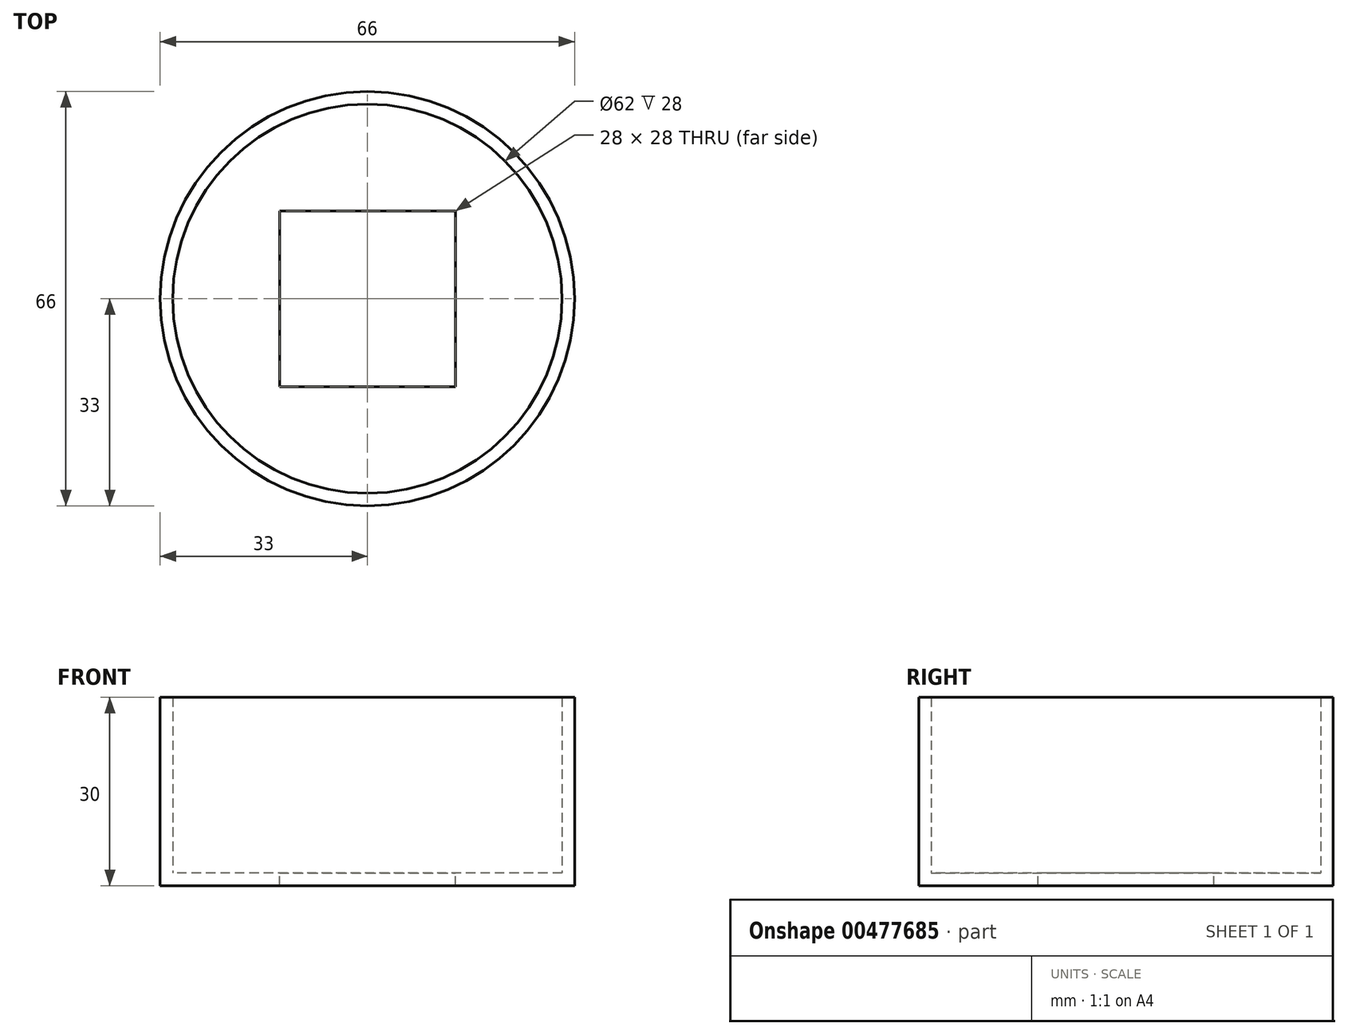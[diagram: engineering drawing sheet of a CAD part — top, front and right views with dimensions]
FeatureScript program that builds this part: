
annotation { "Feature Type Name" : "Feature", "Feature Type Description" : "" }
export const myFeature = defineFeature(function(context is Context, id is Id, definition is map)
    precondition{}
    {
        {
            var Q0;
            Q0=qCreatedBy(makeId("Top.planeOp"),FACE);
            var sketch = newSketch(context, id + "F0", { "sketchPlane" : qUnion([Q0])});
            skCircle(sketch, "E0", {"center": v(0, 0) * mm, "radius": 33 * mm});
            skSolve(sketch);
        }
        {
            var Q0;
            Q0=qSketchRegion(id+"F0",true);
            extrude(context, id + "F1", {"entities" : qUnion([Q0]), "depth" : 30 * mm});
        }
        {
            var Q0;
            Q0=makeQuery(id+"F1.opExtrude","CAP_FACE",FACE,{"disambiguationData":[OSD([sQuery(id+"F0.wireOp",EDGE,"E0")])],"isStart":false});
            shell(context, id + "F2", {"entities" : qUnion([Q0]), "thickness" : 2 * mm});
        }
        {
            var Q0;
            Q0=qSketchRegion(id+"F0",true);
            extrude(context, id + "F3", {"entities" : qUnion([Q0]), "operationType" : NewBodyOperationType.REMOVE, "endBound" : BoundingType.THROUGH_ALL, "oppositeDirection" : true, "depth" : 25 * mm});
        }
        {
            var Q0;
            Q0=makeQuery(id+"F0.imprint","IMPRINT",FACE,{"disambiguationData":[TD([[makeQuery(id+"F0.imprint","IMPRINT",EDGE,{"derivedFrom":sQuery(id+"F0.wireOp",EDGE,"E0")}),1.0]])]});
            var sketch = newSketch(context, id + "F4", { "sketchPlane" : qUnion([Q0])});
            skLineSegment(sketch, "E1.bottom", {"start": v(-14, 14) * mm, "end": v(14, 14) * mm});
            skLineSegment(sketch, "E1.top", {"start": v(-14, -14) * mm, "end": v(14, -14) * mm});
            skLineSegment(sketch, "E1.left", {"start": v(-14, 14) * mm, "end": v(-14, -14) * mm});
            skLineSegment(sketch, "E1.right", {"start": v(14, 14) * mm, "end": v(14, -14) * mm});
            skPoint(sketch, "E1.middle", {"position": v(0, 0) * mm});
            skSolve(sketch);
        }
        {
            var Q0;
            Q0=makeQuery(id+"F4.imprint","IMPRINT",FACE,{"disambiguationData":[TD([[makeQuery(id+"F4.imprint","IMPRINT",EDGE,{"derivedFrom":sQuery(id+"F4.wireOp",EDGE,"E1.bottom")}),-1.0]])]});
            extrude(context, id + "F5", {"entities" : qUnion([Q0]), "operationType" : NewBodyOperationType.REMOVE, "endBound" : BoundingType.SYMMETRIC, "oppositeDirection" : true, "depth" : 25 * mm});
        }
    });
